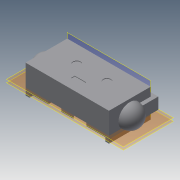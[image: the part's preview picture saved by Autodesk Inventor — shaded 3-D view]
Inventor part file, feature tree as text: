
AUTODESK INVENTOR PART (.ipt)
format: ipt  version: 2014 (Build 180170000, 170)  size: 270,848 bytes
history: native  units: mm
features: extrude x13, sketch x13, other x4, fillet x3
ambient origin geometry x8: Origin, YZ Plane, XZ Plane, XY Plane, X Axis, Y Axis, Z Axis, Center Point
bodies: Body1 (feature_tree)
feature tree (33):
  other  "ソリッド1"
  extrude  "押し出し1"  Depth=44.0mm
  extrude  "押し出し2"  Depth=22.0mm
  fillet  "フィレット1"  Radius=20.0mm
  extrude  "押し出し3"  TaperAngle=0.0deg  [1 undecoded]
  fillet  "フィレット2"  Radius=15.0mm
  other  "作業平面1"
  extrude  "押し出し5"  Depth=12.0mm
  extrude  "押し出し6"  Depth=7.5mm
  extrude  "押し出し7"  Depth=11.0mm
  extrude  "押し出し8"  Depth=6.0mm TaperAngle=0.0deg
  extrude  "押し出し9"  Depth=6.0mm
  extrude  "押し出し10"  Depth=12.0mm
  fillet  "フィレット3"  Radius=11.0mm
  extrude  "押し出し11"  Depth=7.5mm
  other  "作業平面2"
  extrude  "押し出し12"  Depth=6.0mm TaperAngle=0.0deg
  other  "作業平面3"
  extrude  "押し出し13"  Depth=6.0mm
  extrude  "押し出し14"  Depth=2.0mm
  sketch  "スケッチ1"
  sketch  "スケッチ2"
  sketch  "スケッチ3"
  sketch  "スケッチ5"
  sketch  "スケッチ6"
  sketch  "スケッチ7"
  sketch  "スケッチ8"
  sketch  "スケッチ9"
  sketch  "スケッチ10"
  sketch  "スケッチ11"
  sketch  "スケッチ12"
  sketch  "スケッチ13"
  sketch  "スケッチ14"
note: 1 required parameter value undecoded (feature->parameter linkage not recoverable at this tier; creation-order binding heuristic only, values carry confidence <= 0.55)
